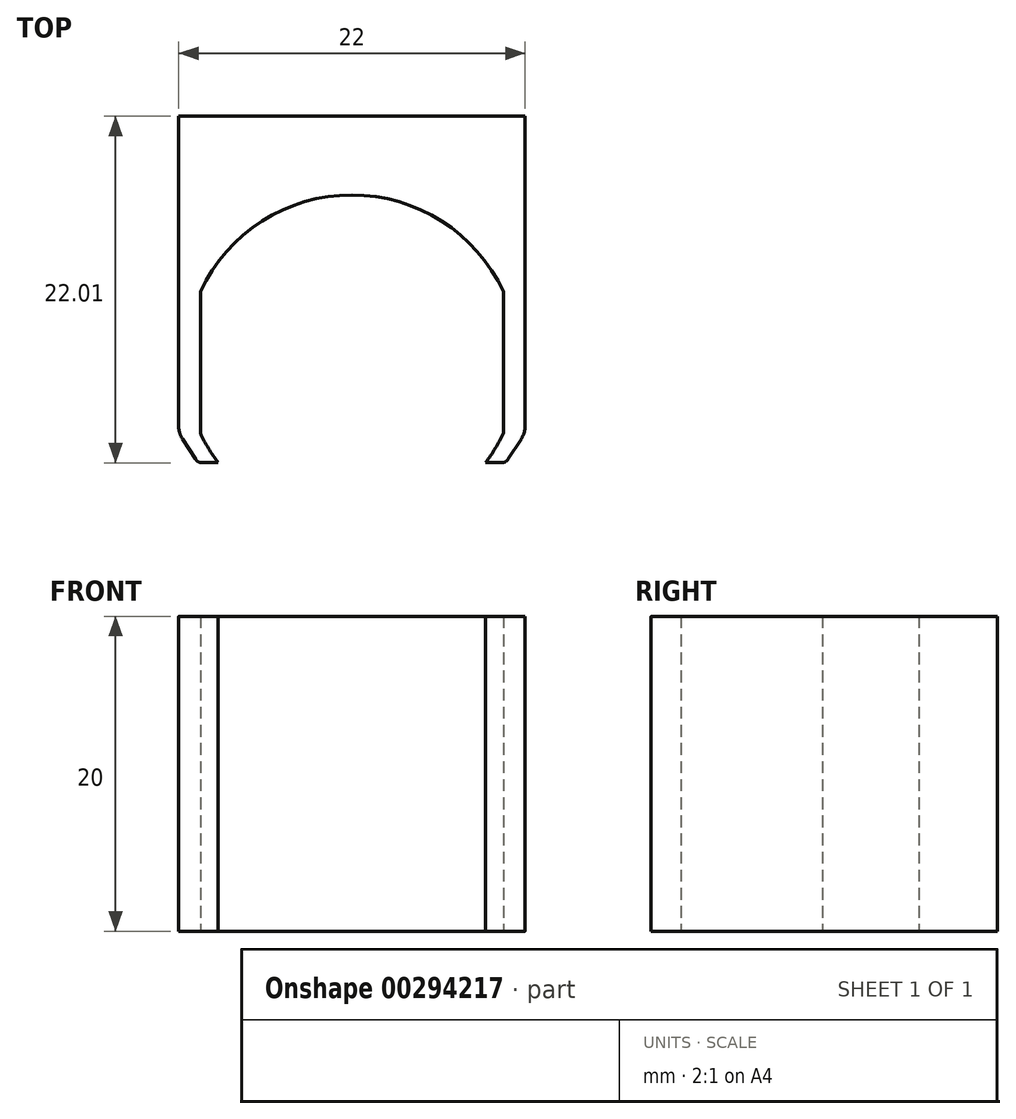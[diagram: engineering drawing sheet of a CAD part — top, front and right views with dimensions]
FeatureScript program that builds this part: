
annotation { "Feature Type Name" : "Feature", "Feature Type Description" : "" }
export const myFeature = defineFeature(function(context is Context, id is Id, definition is map)
    precondition{}
    {
        {
            var Q0;
            Q0=qCreatedBy(makeId("Top.planeOp"),FACE);
            var sketch = newSketch(context, id + "F0", { "sketchPlane" : qUnion([Q0])});
            skArc(sketch, "E0", {"start": v(8.5, -6.39) * mm, "mid": v(0, 10.62) * mm, "end": v(-8.5, -6.39) * mm});
            skLineSegment(sketch, "E1.left", {"start": v(9.62, -4.5) * mm, "end": v(9.62, 4.5) * mm});
            skLineSegment(sketch, "E1.right", {"start": v(-9.62, -4.5) * mm, "end": v(-9.62, 4.5) * mm});
            skPoint(sketch, "E2", {"position": v(-8.5, -6.39) * mm});
            skPoint(sketch, "E3", {"position": v(8.5, -6.39) * mm});
            skLineSegment(sketch, "E4", {"start": v(-10.76, -4.87) * mm, "end": v(-9.78, -6.39) * mm});
            skLineSegment(sketch, "E5", {"start": v(-9.78, -6.39) * mm, "end": v(-8.5, -6.39) * mm});
            skLineSegment(sketch, "E6", {"start": v(10.76, -4.87) * mm, "end": v(9.78, -6.39) * mm});
            skLineSegment(sketch, "E7", {"start": v(9.78, -6.39) * mm, "end": v(8.5, -6.39) * mm});
            skLineSegment(sketch, "E8", {"start": v(-11, 15.62) * mm, "end": v(-11, -4.06) * mm});
            skLineSegment(sketch, "E9", {"start": v(11, 15.62) * mm, "end": v(11, -4.06) * mm});
            skLineSegment(sketch, "E10", {"start": v(-11, 15.62) * mm, "end": v(11, 15.62) * mm});
            skPoint(sketch, "E11", {"position": v(0, 10.62) * mm});
            skPoint(sketch, "E12", {"position": v(0, 15.62) * mm});
            skPoint(sketch, "E13.visualSharp", {"position": v(-11, -4.5) * mm});
            skArc(sketch, "E13.filletArc", {"start": v(-11, -4.06) * mm, "mid": v(-10.94, -4.48) * mm, "end": v(-10.76, -4.87) * mm});
            skPoint(sketch, "E14.visualSharp", {"position": v(11, -4.5) * mm});
            skArc(sketch, "E14.filletArc", {"start": v(10.76, -4.87) * mm, "mid": v(10.94, -4.48) * mm, "end": v(11, -4.06) * mm});
            skSolve(sketch);
        }
        {
            var Q0;
            Q0=makeQuery(id+"F0.imprint","IMPRINT",FACE,{"disambiguationData":[TD([[makeQuery(id+"F0.imprint","IMPRINT",EDGE,{"derivedFrom":sQuery(id+"F0.wireOp",EDGE,"E4")}),1.0]])]});
            var Q1;
            {var subQ0=sQuery(id+"F0.wireOp",EDGE,"E1.right");Q1=makeQuery(id+"F0.imprint","IMPRINT",FACE,{"disambiguationData":[TD([[makeQuery(id+"F0.imprint","IMPRINT",EDGE,{"derivedFrom":subQ0}),1.0]])]});}
            var Q2;
            {var subQ0=sQuery(id+"F0.wireOp",EDGE,"E1.left");Q2=makeQuery(id+"F0.imprint","IMPRINT",FACE,{"disambiguationData":[TD([[makeQuery(id+"F0.imprint","IMPRINT",EDGE,{"derivedFrom":subQ0}),-1.0]])]});}
            extrude(context, id + "F1", {"entities" : qUnion([Q0, Q1, Q2]), "depth" : 20 * mm});
        }
        {
            var Q0;
            Q0=makeQuery(id+"F1.opExtrude","SWEPT_EDGE",EDGE,{"disambiguationData":[OSD([sQuery(id+"F0.wireOp",EDGE,"E4"),sQuery(id+"F0.wireOp",EDGE,"E5")])]});
            var Q1;
            Q1=makeQuery(id+"F1.opExtrude","SWEPT_EDGE",EDGE,{"disambiguationData":[OSD([sQuery(id+"F0.wireOp",EDGE,"E6"),sQuery(id+"F0.wireOp",EDGE,"E7")])]});
            fillet(context, id + "F2", {"entities" : qUnion([Q0, Q1]), "radius" : .5 * mm, "tangentPropagation" : true, "allowEdgeOverflow" : false});
        }
    });
